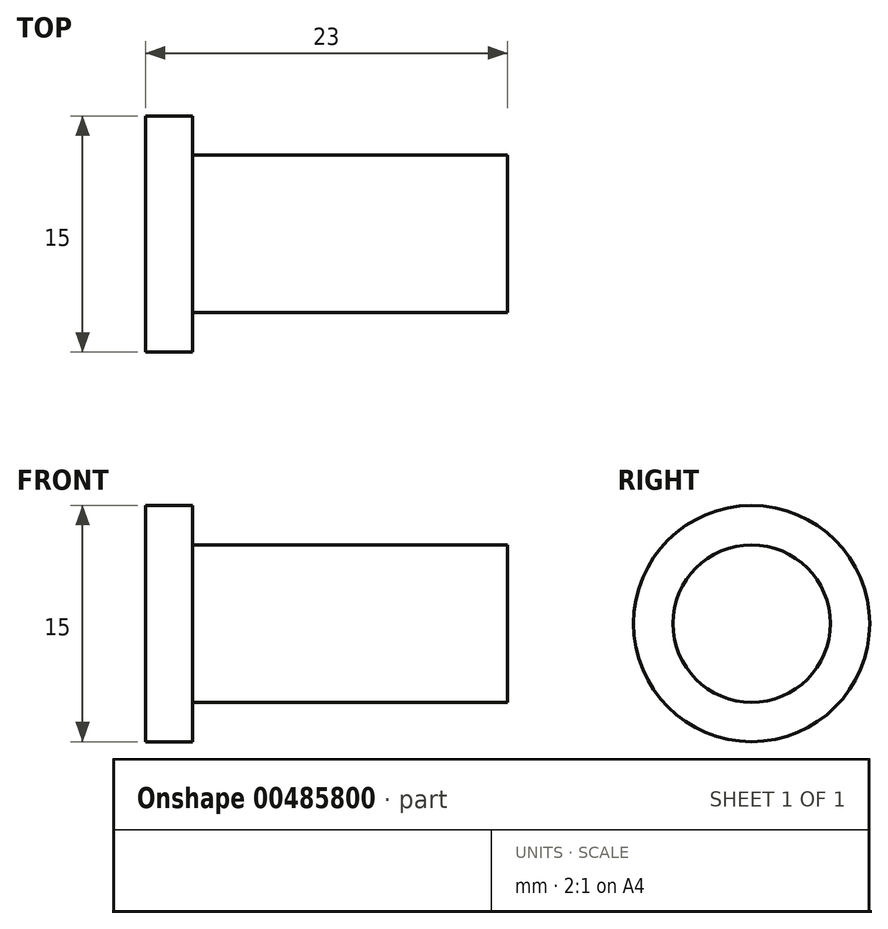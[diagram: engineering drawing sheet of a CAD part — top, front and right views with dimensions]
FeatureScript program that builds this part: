
annotation { "Feature Type Name" : "Feature", "Feature Type Description" : "" }
export const myFeature = defineFeature(function(context is Context, id is Id, definition is map)
    precondition{}
    {
        {
            var Q0;
            Q0=qCreatedBy(makeId("Top.planeOp"),FACE);
            var sketch = newSketch(context, id + "F0", { "sketchPlane" : qUnion([Q0])});
            skLineSegment(sketch, "E0.bottom", {"start": v(23, 0) * mm, "end": v(0, 0) * mm});
            skLineSegment(sketch, "E0.top", {"start": v(3, 7.5) * mm, "end": v(0, 7.5) * mm});
            skLineSegment(sketch, "E0.left", {"start": v(0, 7.5) * mm, "end": v(0, 0) * mm});
            skLineSegment(sketch, "E0.right", {"start": v(23, 5) * mm, "end": v(23, 0) * mm});
            skLineSegment(sketch, "E1.top", {"start": v(23, 5) * mm, "end": v(3, 5) * mm});
            skLineSegment(sketch, "E1.right", {"start": v(3, 7.5) * mm, "end": v(3, 5) * mm});
            skSolve(sketch);
        }
        {
            var Q0;
            Q0 = qSketchRegion(id + "F0", true);
            var Q1;
            Q1=sQuery(id+"F0.wireOp",EDGE,"E0.bottom");
            revolve(context, id + "F1", {"entities" : qUnion([Q0]), "axis" : qUnion([Q1]), "revolveType" : RevolveType.FULL});
        }
    });
